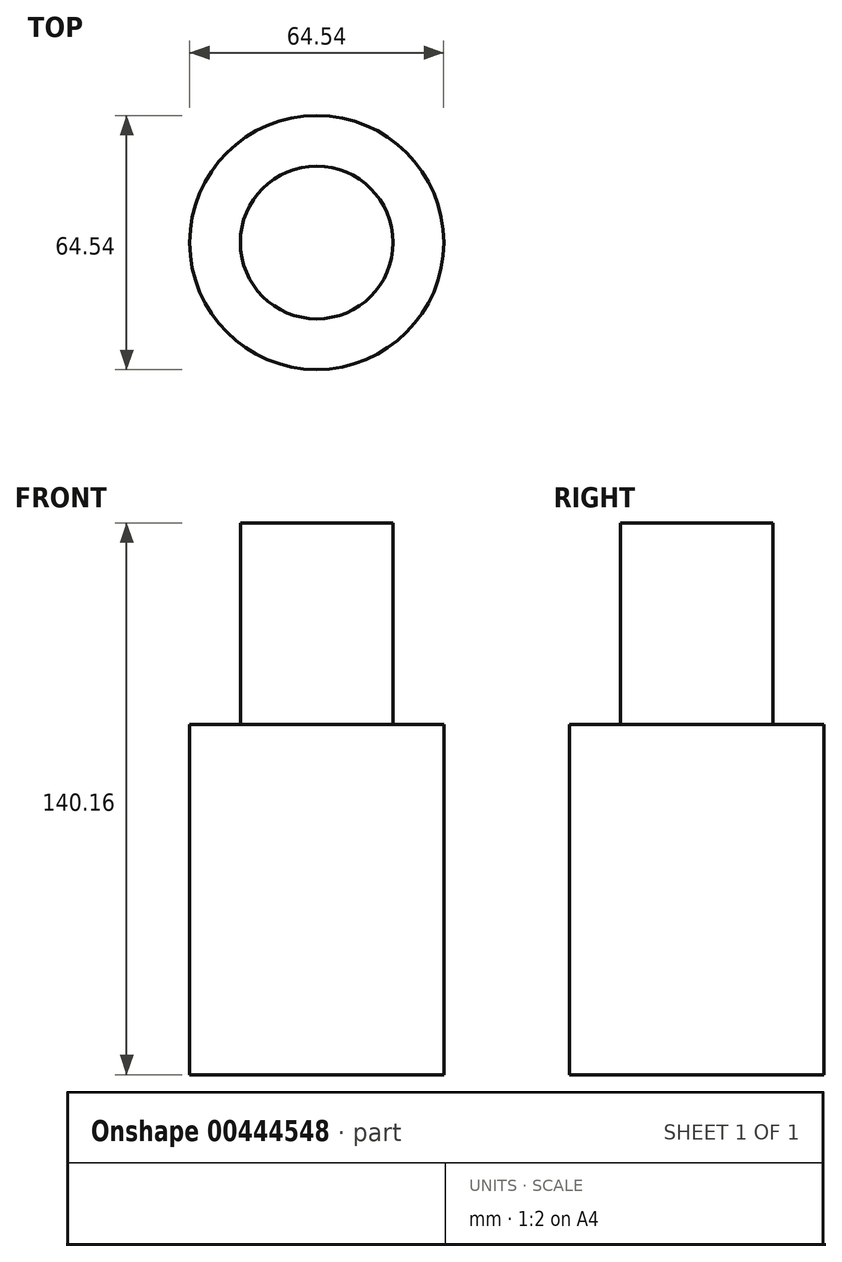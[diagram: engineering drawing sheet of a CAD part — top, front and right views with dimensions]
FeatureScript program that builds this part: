
annotation { "Feature Type Name" : "Feature", "Feature Type Description" : "" }
export const myFeature = defineFeature(function(context is Context, id is Id, definition is map)
    precondition{}
    {
        {
            var Q0;
            Q0=qCreatedBy(makeId("Front.planeOp"),FACE);
            var sketch = newSketch(context, id + "F0", { "sketchPlane" : qUnion([Q0])});
            skLineSegment(sketch, "E0.bottom", {"start": v(0, 44.27) * mm, "end": v(32.27, 44.27) * mm});
            skLineSegment(sketch, "E0.top", {"start": v(0, -44.7) * mm, "end": v(32.27, -44.7) * mm});
            skLineSegment(sketch, "E0.left", {"start": v(0, 44.27) * mm, "end": v(0, -44.7) * mm});
            skLineSegment(sketch, "E0.right", {"start": v(32.27, 44.27) * mm, "end": v(32.27, -44.7) * mm});
            skSolve(sketch);
        }
        {
            var Q0;
            Q0 = qSketchRegion(id + "F0", true);
            var Q1;
            Q1=makeQuery(id+"F0.imprint","IMPRINT",FACE,{"disambiguationData":[TD([[makeQuery(id+"F0.imprint","IMPRINT",EDGE,{"derivedFrom":sQuery(id+"F0.wireOp",EDGE,"E0.bottom")}),-1.0]])]});
            var Q2;
            Q2=sQuery(id+"F0.wireOp",EDGE,"E0.left");
            revolve(context, id + "F1", {"entities" : qUnion([Q0, Q1]), "axis" : qUnion([Q2]), "revolveType" : RevolveType.FULL});
        }
        {
            var Q0;
            Q0=makeQuery(id+"F1.opRevolve","SWEPT_FACE",FACE,{"disambiguationData":[OSD([sQuery(id+"F0.wireOp",EDGE,"E0.bottom")])]});
            var sketch = newSketch(context, id + "F2", { "sketchPlane" : qUnion([Q0])});
            skCircle(sketch, "E1", {"center": v(0, 0) * mm, "radius": 19.4 * mm});
            skSolve(sketch);
        }
        {
            var Q0;
            Q0 = qSketchRegion(id + "F2", true);
            extrude(context, id + "F3", {"entities" : qUnion([Q0]), "operationType" : NewBodyOperationType.ADD, "depth" : 51.2 * mm});
        }
    });
